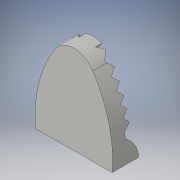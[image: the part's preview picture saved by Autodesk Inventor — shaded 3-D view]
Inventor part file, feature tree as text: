
AUTODESK INVENTOR PART (.ipt)
format: ipt  version: 2016 (Build 200138000, 138)  size: 441,856 bytes
history: native  units: in
note: dims shown in document units (in); Inventor stores cm internally (conversion verified against a paired STEP export)
features: sketch x23, extrude x22, other x12, plane x12, projected_geometry x8, reference x4
ambient origin geometry x8: Origin, YZ Plane, XZ Plane, XY Plane, X Axis, Y Axis, Z Axis, Center Point
bodies: Solid1 (feature_tree)
feature tree (81):
  extrude  "Extrusion1"  Depth=1.0in
  extrude  "Extrusion2"  Depth=0.3937in TaperAngle=0.0deg
  extrude  "Extrusion3"  Depth=1.0in
  extrude  "Extrusion4"  Depth=1.0in TaperAngle=0.0deg
  sketch  "Sketch5"  dims[d12=1.0in d13=0.0in d15=0.5in]
  other  "Work Point1"
  other  "Work Point2"
  other  "Work Point3"
  other  "Work Point4"
  other  "Work Point5"
  other  "Work Point6"
  other  "Work Point7"
  other  "Work Point8"
  other  "Work Point9"
  other  "Work Point10"
  other  "Work Point11"
  other  "Work Point12"
  plane  "Work Plane1"
  plane  "Work Plane2"
  plane  "Work Plane3"
  plane  "Work Plane4"
  plane  "Work Plane5"
  plane  "Work Plane6"
  sketch  "Sketch6"  dims[d16=2.3622in d18=0.45in d19=0.3937in d21=1.0in d23=0.25in]
  sketch  "Sketch7"  dims[d24=0.5in d25=0.25in]
  sketch  "Sketch8"  dims[d26=0.25in d27=0.5in d28=0.25in d29=0.25in d30=0.5in d31=0.25in]
  sketch  "Sketch9"  dims[d32=0.25in d33=0.5in d34=0.25in d35=0.25in d36=0.5in d37=0.25in]
  sketch  "Sketch10"  dims[d38=0.25in d39=0.5in d40=0.25in d44=1.0in d45=0.0in]
  sketch  "Sketch11"  dims[d46=1.0in d47=0.0in d48=1.0in d49=0.0in]
  extrude  "Extrusion5"  Depth=0.5in
  extrude  "Extrusion6"  Depth=0.3937in
  extrude  "Extrusion7"  Depth=0.25in
  extrude  "Extrusion8"  Depth=0.25in
  extrude  "Extrusion9"  Depth=0.25in
  extrude  "Extrusion10"  Depth=1.0in TaperAngle=0.0deg
  plane  "Work Plane7"
  plane  "Work Plane8"
  plane  "Work Plane9"
  plane  "Work Plane10"
  plane  "Work Plane11"
  plane  "Work Plane12"
  sketch  "Sketch13"  dims[d50=1.0in d51=0.0in d52=1.0in d53=0.0in]
  sketch  "Sketch14"  dims[d54=1.0in d55=0.0in d56=0.25in]
  sketch  "Sketch15"  dims[d57=0.5in d58=0.25in]
  sketch  "Sketch16"  dims[d59=0.25in d60=0.5in d61=0.25in d62=0.25in d63=0.5in d64=0.25in]
  sketch  "Sketch17"  dims[d65=0.25in d66=0.5in d67=0.25in d68=0.25in d69=0.5in d70=0.25in]
  sketch  "Sketch18"  dims[d71=0.25in d72=0.5in d73=0.25in d74=1.0in d75=0.0in]
  extrude  "Extrusion11"  Depth=1.0in TaperAngle=0.0deg
  extrude  "Extrusion12"  Depth=1.0in TaperAngle=0.0deg
  extrude  "Extrusion13"  Depth=0.25in
  extrude  "Extrusion14"  Depth=0.25in
  extrude  "Extrusion15"  Depth=0.25in
  extrude  "Extrusion16"  Depth=0.25in
  extrude  "Extrusion17"  Depth=1.0in TaperAngle=0.0deg
  extrude  "Extrusion18"  Depth=1.0in TaperAngle=0.0deg
  extrude  "Extrusion19"  Depth=1.0in TaperAngle=0.0deg
  extrude  "Extrusion20"  Depth=1.0in TaperAngle=0.0deg
  extrude  "Extrusion21"  Depth=0.3937in
  extrude  "Extrusion22"  Depth=0.3937in
  sketch  "Sketch1"  dims[d0=4.5in d1=1.0in]
  reference  "Reference1"
  sketch  "Sketch2"  dims[d2=0.1969in d3=0.0in d4=0.3937in d5=0.0in]
  projected_geometry  "Projected Loop1"
  sketch  "Sketch3"  dims[d6=0.9843in d7=1.0in]
  sketch  "Sketch4"  dims[d8=4.0in d9=0.0in d10=1.0in d11=0.0in]
  projected_geometry  "Projected Loop2"
  projected_geometry  "Projected Loop3"
  sketch  "Sketch19"  dims[d76=1.0in d77=0.0in d78=1.0in d79=0.0in]
  projected_geometry  "Projected Loop4"
  sketch  "Sketch20"  dims[d80=1.0in d81=0.0in d82=1.0in d83=0.0in]
  reference  "Reference2"
  sketch  "Sketch21"  dims[d84=1.0in d85=0.0in d86=1.0in d87=0.0in]
  reference  "Reference3"
  reference  "Reference4"
  sketch  "Sketch22"  dims[d88=4.0in d89=0.0in d90=0.3937in]
  sketch  "Sketch23"  dims[d91=0.3937in d92=0.0787in]
  projected_geometry  "Projected Loop5"
  projected_geometry  "Projected Loop6"
  projected_geometry  "Projected Loop7"
  sketch  "Sketch24"  dims[d93=0.0787in d94=0.1969in d95=0.7874in d96=0.1969in d97=0.7874in d98=1.2402in d99=0.0in d100=0.1969in d101=0.1378in d102=1.5748in d103=0.0in d104=1.5748in d105=0.0in d106=0.2953in d107=0.0in]
  projected_geometry  "Projected Loop8"
